# Revit family: 2071155
name_source: partatom
category: Lighting Fixtures
revit_build: Autodesk Revit 2018 (Build: 20170223_1515(x64)
units: mm (PartAtom-declared; Revit-internal decimal feet)

## family parameters
Cut with Voids When Loaded = No
Host = Face
Light Source = Yes
OmniClass Number = 23.80.70.00
OmniClass Title = Lighting
Part Type = Normal
Room Calculation Point = No
Round Connector Dimension = Use Diameter
Shared = No

## types (1)
- 2071155 COLOSSAL 400 940 OP DIR+H WHT SSC
    Apparent Load = 21 VA
    Assembly Code = D5020200
    AssetType = Fixed
    ClassificationName = Uniclass2015
    ClassificationValue = EF_70_80
    Color Filter = 16777215
    Cost = 0 $
    Default Elevation = 1219 mm
    Description = 400mm diameter circular architectural luminaire, can be surface mounted or suspended. Powder coated aluminium housing (RAL9016) with polycarbonate opal diffuser. Direct/indirect (halo) light distribution, 2280lm luminuous flux, 20.5W system power, 111lm/W luminiaire efficacy. Sylsmart Standalone enabled. Colour rendering index Ra >90, 4000K Neutral White LED, chromaticity tolerance of 3-step MacAdam ellipse. IP40, IK03. 450mA drive current. Electrical protection Class1, 220-240V. Reported lifetime 66k hours L90B10.
    Dimming Lamp Color Temperature Shift = <None>
    DocumentationLiterature = http://www.sylvania-lighting.com
    ElectricShockClassification = 111
    Emit Shape Visible in Rendering = No
    Emit from Circle Diameter = 385 mm  [stored 1.26312 ft]
    IfcExportAs = Class I
    IfcExportType = IfcLightFixtureType
    ImpactProtectionIndex = IfcLightFixtureType
    IngressProtection = IfcLightFixtureType
    InputNominalFrequency = 4000
    InputVoltage = 0
    LampColourRenderingIndex = 16500
    LampColourTemperature = LED
    LampMacAdamStep = 90
    LampNominalLuminous = 4000 K
    LightOutputRatio = LED
    LuminaireType = 0
    ManufacturerName = 111 lm/W
    Material = Feilo Sylvania
    Material_1_SYL = Polycarbonate_Sylvania_Opal
    Material_2_SYL = Polycarbonate_Sylvania_White
    Material_3_SYL = LED-Sylvania
    Material_4_SYL = <By Category>
    Model = COLOSSAL 400mm 940 OPAL DIR+HAL WHITE SSC
    ModelNumber = 2071155
    ModelReference = COLOSSAL 400mm 940 OPAL DIR+HAL WHITE SSC
    Name = COLOSSAL 400mm 940 OPAL DIR+HAL WHITE SSC
    NominalDepth = 400 mm  [stored 1.31234 ft]
    NominalHeight = 93 mm  [stored 0.305118 ft]
    NominalLength = 400 mm  [stored 1.31234 ft]
    Photometric Web File = 2071155.ies
    PowerConsumption = Lighting
    PowerFactor = 0
    Tilt Angle = -90.00°
    Type Image = <None>
    TypeName = COLOSSAL 400mm 940 OPAL DIR+HAL WHITE SSC
    URL = 0.95
    Voltage = 230 V
    WarrantyDescription = http://www.sylvania-lighting.com
    iner diameter = 390 mm  [stored 1.27953 ft]

note: [stored X ft] marks values corroborated as IEEE doubles in the binary element streams (Revit-internal decimal feet)

## geometry (parser evidence)
native form markers: Sweep x3
no freeform markers — native parametric forms only
